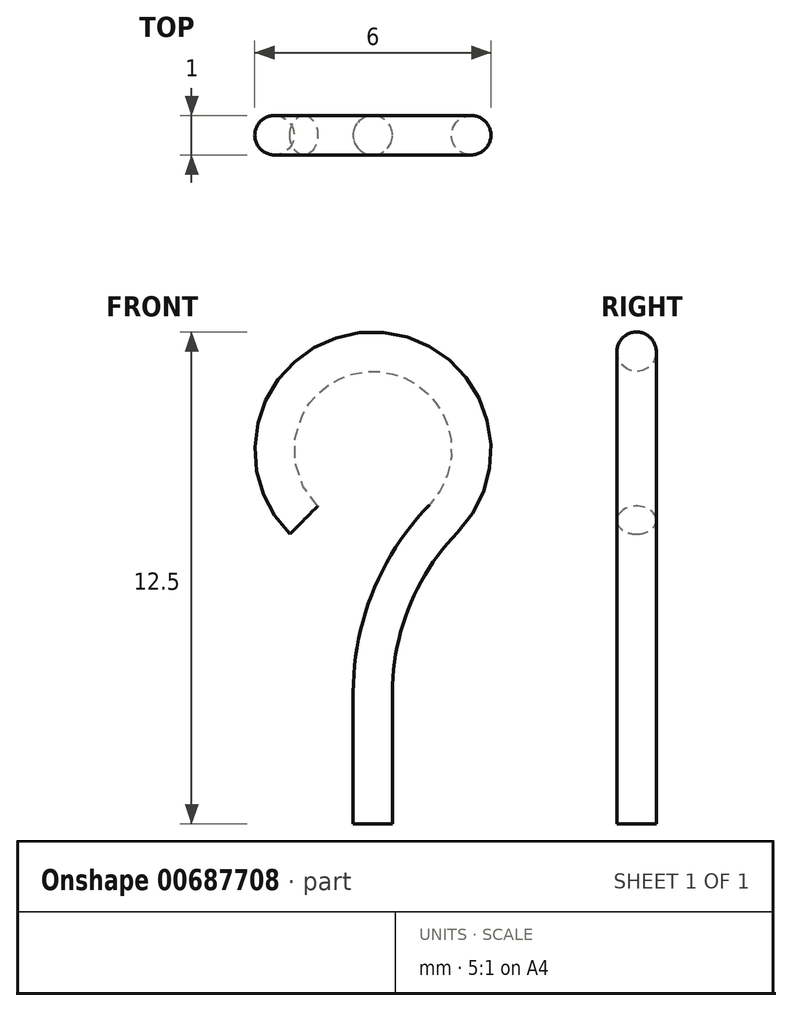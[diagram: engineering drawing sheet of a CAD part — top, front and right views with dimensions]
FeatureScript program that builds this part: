
annotation { "Feature Type Name" : "Feature", "Feature Type Description" : "" }
export const myFeature = defineFeature(function(context is Context, id is Id, definition is map)
    precondition{}
    {
        {
            var Q0;
            Q0=qCreatedBy(makeId("Front.planeOp"),FACE);
            var sketch = newSketch(context, id + "F0", { "sketchPlane" : qUnion([Q0])});
            skLineSegment(sketch, "E0", {"start": v(0, 0) * mm, "end": v(0, 3.34) * mm});
            skArc(sketch, "E1", {"start": v(1.8, 7.76) * mm, "mid": v(-0.03, 12) * mm, "end": v(-1.75, 7.72) * mm});
            skLineSegment(sketch, "E2", {"start": v(0, 9.5) * mm, "end": v(-1.75, 7.72) * mm});
            skPoint(sketch, "E3.visualSharp", {"position": v(0, 7) * mm});
            skArc(sketch, "E3.filletArc", {"start": v(1.8, 7.76) * mm, "mid": v(0.47, 5.72) * mm, "end": v(0, 3.34) * mm});
            skSolve(sketch);
        }
        {
            var Q0;
            Q0=qCreatedBy(makeId("Top.planeOp"),FACE);
            var sketch = newSketch(context, id + "F1", { "sketchPlane" : qUnion([Q0])});
            skCircle(sketch, "E4", {"center": v(0, 0) * mm, "radius": 0.5 * mm});
            skSolve(sketch);
        }
        {
            var Q0;
            Q0=makeQuery(id+"F1.imprint","IMPRINT",FACE,{"disambiguationData":[TD([[makeQuery(id+"F1.imprint","IMPRINT",EDGE,{"derivedFrom":sQuery(id+"F1.wireOp",EDGE,"E4")}),1.0]])]});
            var Q1;
            Q1=sQuery(id+"F0.wireOp",EDGE,"E0");
            var Q2;
            Q2=sQuery(id+"F0.wireOp",EDGE,"E3.filletArc");
            var Q3;
            Q3=sQuery(id+"F0.wireOp",EDGE,"E1");
            sweep(context, id + "F2", {"profiles" : qUnion([Q0]), "path" : qUnion([Q1, Q2, Q3])});
        }
    });
